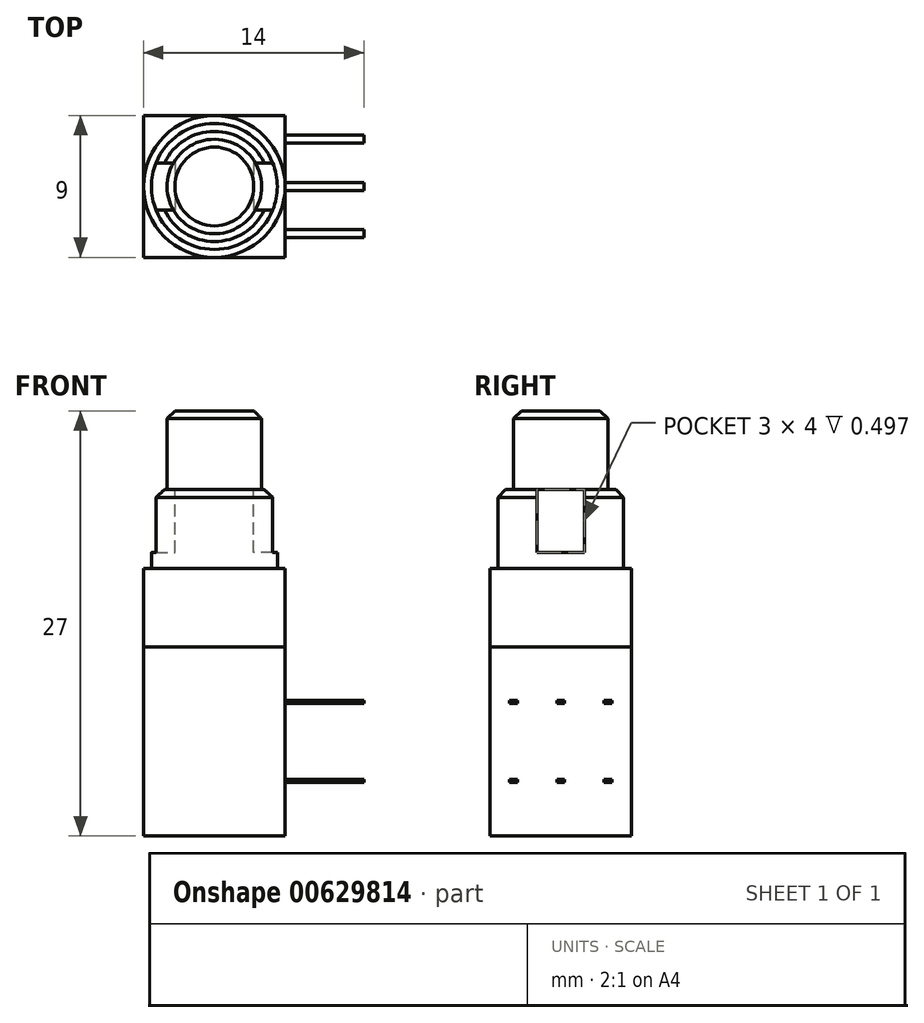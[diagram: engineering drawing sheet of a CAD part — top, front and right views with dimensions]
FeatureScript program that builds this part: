
annotation { "Feature Type Name" : "Feature", "Feature Type Description" : "" }
export const myFeature = defineFeature(function(context is Context, id is Id, definition is map)
    precondition{}
    {
        {
            var Q0;
            Q0=qCreatedBy(makeId("Top.planeOp"),FACE);
            var sketch = newSketch(context, id + "F0", { "sketchPlane" : qUnion([Q0])});
            skLineSegment(sketch, "E0.bottom", {"start": v(4.5, 4.5) * mm, "end": v(-4.5, 4.5) * mm});
            skLineSegment(sketch, "E0.top", {"start": v(4.5, -4.5) * mm, "end": v(-4.5, -4.5) * mm});
            skLineSegment(sketch, "E0.left", {"start": v(4.5, 4.5) * mm, "end": v(4.5, -4.5) * mm});
            skLineSegment(sketch, "E0.right", {"start": v(-4.5, 4.5) * mm, "end": v(-4.5, -4.5) * mm});
            skPoint(sketch, "E0.middle", {"position": v(0, 0) * mm});
            skSolve(sketch);
        }
        {
            var Q0;
            Q0=makeQuery(id+"F0.imprint","IMPRINT",FACE,{"disambiguationData":[TD([[makeQuery(id+"F0.imprint","IMPRINT",EDGE,{"derivedFrom":sQuery(id+"F0.wireOp",EDGE,"E0.bottom")}),1.0]])]});
            extrude(context, id + "F1", {"entities" : qUnion([Q0]), "depth" : 12 * mm, "offsetDistance" : 25 * mm});
        }
        {
            var Q0;
            Q0=makeQuery(id+"F1.opExtrude","CAP_FACE",FACE,{"disambiguationData":[OSD([sQuery(id+"F0.wireOp",EDGE,"E0.bottom"),sQuery(id+"F0.wireOp",EDGE,"E0.top"),sQuery(id+"F0.wireOp",EDGE,"E0.left"),sQuery(id+"F0.wireOp",EDGE,"E0.right")])],"isStart":false});
            var sketch = newSketch(context, id + "F2", { "sketchPlane" : qUnion([Q0])});
            skCircle(sketch, "E1", {"center": v(0, 0) * mm, "radius": 4.5 * mm});
            skSolve(sketch);
        }
        {
            var Q0;
            {var subQ0=sQuery(id+"F2.wireOp",EDGE,"E1");var subQ1=makeQuery(id+"F2.imprint","INTERSECT",VERTEX,{"derivedFrom":[makeQuery(id+"F1.opExtrude","CAP_EDGE",EDGE,{"disambiguationData":[OSD([sQuery(id+"F0.wireOp",EDGE,"E0.bottom")])],"isStart":false}),subQ0]});Q0=makeQuery(id+"F2.imprint","IMPRINT",FACE,{"disambiguationData":[TD([[makeQuery(id+"F2.imprint","IMPRINT",EDGE,{"disambiguationData":[TD([[subQ1,1.0]])],"derivedFrom":subQ0}),1.0]])]});}
            extrude(context, id + "F3", {"entities" : qUnion([Q0]), "operationType" : NewBodyOperationType.ADD, "depth" : 5 * mm, "offsetDistance" : 25 * mm});
        }
        {
            var Q0;
            Q0=makeQuery(id+"F3.opExtrude","CAP_FACE",FACE,{"disambiguationData":[OSD([sQuery(id+"F2.wireOp",EDGE,"E1")])],"isStart":false});
            var sketch = newSketch(context, id + "F4", { "sketchPlane" : qUnion([Q0])});
            skCircle(sketch, "E2", {"center": v(0, 0) * mm, "radius": 4 * mm});
            skSolve(sketch);
        }
        {
            var Q0;
            Q0=makeQuery(id+"F4.imprint","IMPRINT",FACE,{"disambiguationData":[TD([[makeQuery(id+"F4.imprint","IMPRINT",EDGE,{"derivedFrom":sQuery(id+"F4.wireOp",EDGE,"E2")}),1.0]])]});
            extrude(context, id + "F5", {"entities" : qUnion([Q0]), "operationType" : NewBodyOperationType.ADD, "depth" : 5 * mm, "offsetDistance" : 25 * mm});
        }
        {
            var Q0;
            Q0=makeQuery(id+"F5.opExtrude","CAP_FACE",FACE,{"disambiguationData":[OSD([sQuery(id+"F4.wireOp",EDGE,"E2")])],"isStart":false});
            var sketch = newSketch(context, id + "F6", { "sketchPlane" : qUnion([Q0])});
            skCircle(sketch, "E3.0", {"center": v(0, 0) * mm, "radius": 4 * mm});
            skLineSegment(sketch, "E4", {"start": v(-3.7, 1.5) * mm, "end": v(-2.5, 1.5) * mm});
            skLineSegment(sketch, "E5", {"start": v(-2.5, 1.5) * mm, "end": v(-2.5, -1.5) * mm});
            skLineSegment(sketch, "E6", {"start": v(-2.5, -1.5) * mm, "end": v(-3.7, -1.5) * mm});
            skLineSegment(sketch, "E7", {"start": v(3.7, 1.5) * mm, "end": v(2.5, 1.5) * mm});
            skLineSegment(sketch, "E8", {"start": v(2.5, 1.5) * mm, "end": v(2.5, -1.5) * mm});
            skLineSegment(sketch, "E9", {"start": v(2.5, -1.5) * mm, "end": v(3.7, -1.5) * mm});
            skSolve(sketch);
        }
        {
            var Q0;
            {var subQ0=sQuery(id+"F6.wireOp",EDGE,"E4");Q0=makeQuery(id+"F6.imprint","IMPRINT",FACE,{"disambiguationData":[TD([[makeQuery(id+"F6.imprint","IMPRINT",EDGE,{"derivedFrom":subQ0}),-1.0]])]});}
            var Q1;
            {var subQ0=sQuery(id+"F6.wireOp",EDGE,"E7");Q1=makeQuery(id+"F6.imprint","IMPRINT",FACE,{"disambiguationData":[TD([[makeQuery(id+"F6.imprint","IMPRINT",EDGE,{"derivedFrom":subQ0}),1.0]])]});}
            extrude(context, id + "F7", {"entities" : qUnion([Q0, Q1]), "operationType" : NewBodyOperationType.REMOVE, "oppositeDirection" : true, "depth" : 4 * mm, "offsetDistance" : 25 * mm});
        }
        {
            var Q0;
            Q0=makeQuery(id+"F5.opExtrude","CAP_FACE",FACE,{"disambiguationData":[OSD([sQuery(id+"F4.wireOp",EDGE,"E2")])],"isStart":false});
            var sketch = newSketch(context, id + "F8", { "sketchPlane" : qUnion([Q0])});
            skCircle(sketch, "E10", {"center": v(0, 0) * mm, "radius": 3 * mm});
            skSolve(sketch);
        }
        {
            var Q0;
            Q0 = qSketchRegion(id + "F8", true);
            extrude(context, id + "F9", {"entities" : qUnion([Q0]), "operationType" : NewBodyOperationType.ADD, "depth" : 5 * mm, "offsetDistance" : 25 * mm});
        }
        {
            var Q0;
            Q0=makeQuery(id+"F1.opExtrude","SWEPT_FACE",FACE,{"disambiguationData":[OSD([sQuery(id+"F0.wireOp",EDGE,"E0.left")])]});
            var sketch = newSketch(context, id + "F10", { "sketchPlane" : qUnion([Q0])});
            skLineSegment(sketch, "E11.bottom", {"start": v(-3, 8.5) * mm, "end": v(3, 8.5) * mm, "construction": true});
            skLineSegment(sketch, "E11.top", {"start": v(-3, 3.5) * mm, "end": v(3, 3.5) * mm, "construction": true});
            skLineSegment(sketch, "E11.left", {"start": v(-3, 8.5) * mm, "end": v(-3, 3.5) * mm, "construction": true});
            skLineSegment(sketch, "E11.right", {"start": v(3, 8.5) * mm, "end": v(3, 3.5) * mm, "construction": true});
            skLineSegment(sketch, "E12", {"start": v(0, 8.5) * mm, "end": v(0, 3.5) * mm, "construction": true});
            skLineSegment(sketch, "E13", {"start": v(0, 3.5) * mm, "end": v(0, 0) * mm, "construction": true});
            skLineSegment(sketch, "E14", {"start": v(3, 6) * mm, "end": v(4.5, 6) * mm, "construction": true});
            skLineSegment(sketch, "E15.bottom", {"start": v(-2.75, 8.4) * mm, "end": v(-3.25, 8.4) * mm});
            skLineSegment(sketch, "E15.top", {"start": v(-2.75, 8.6) * mm, "end": v(-3.25, 8.6) * mm});
            skLineSegment(sketch, "E15.left", {"start": v(-2.75, 8.4) * mm, "end": v(-2.75, 8.6) * mm});
            skLineSegment(sketch, "E15.right", {"start": v(-3.25, 8.4) * mm, "end": v(-3.25, 8.6) * mm});
            skPoint(sketch, "E15.middle", {"position": v(-3, 8.5) * mm});
            skLineSegment(sketch, "E16.bottom", {"start": v(0.25, 8.4) * mm, "end": v(-0.25, 8.4) * mm});
            skLineSegment(sketch, "E16.top", {"start": v(0.25, 8.6) * mm, "end": v(-0.25, 8.6) * mm});
            skLineSegment(sketch, "E16.left", {"start": v(0.25, 8.4) * mm, "end": v(0.25, 8.6) * mm});
            skLineSegment(sketch, "E16.right", {"start": v(-0.25, 8.4) * mm, "end": v(-0.25, 8.6) * mm});
            skPoint(sketch, "E16.middle", {"position": v(0, 8.5) * mm});
            skLineSegment(sketch, "E17.bottom", {"start": v(2.75, 8.4) * mm, "end": v(3.25, 8.4) * mm});
            skLineSegment(sketch, "E17.top", {"start": v(2.75, 8.6) * mm, "end": v(3.25, 8.6) * mm});
            skLineSegment(sketch, "E17.left", {"start": v(2.75, 8.4) * mm, "end": v(2.75, 8.6) * mm});
            skLineSegment(sketch, "E17.right", {"start": v(3.25, 8.4) * mm, "end": v(3.25, 8.6) * mm});
            skPoint(sketch, "E17.middle", {"position": v(3, 8.5) * mm});
            skLineSegment(sketch, "E18.bottom", {"start": v(-3.25, 3.4) * mm, "end": v(-2.75, 3.4) * mm});
            skLineSegment(sketch, "E18.top", {"start": v(-3.25, 3.6) * mm, "end": v(-2.75, 3.6) * mm});
            skLineSegment(sketch, "E18.left", {"start": v(-3.25, 3.4) * mm, "end": v(-3.25, 3.6) * mm});
            skLineSegment(sketch, "E18.right", {"start": v(-2.75, 3.4) * mm, "end": v(-2.75, 3.6) * mm});
            skPoint(sketch, "E18.middle", {"position": v(-3, 3.5) * mm});
            skLineSegment(sketch, "E19.bottom", {"start": v(-0.25, 3.4) * mm, "end": v(0.25, 3.4) * mm});
            skLineSegment(sketch, "E19.top", {"start": v(-0.25, 3.6) * mm, "end": v(0.25, 3.6) * mm});
            skLineSegment(sketch, "E19.left", {"start": v(-0.25, 3.4) * mm, "end": v(-0.25, 3.6) * mm});
            skLineSegment(sketch, "E19.right", {"start": v(0.25, 3.4) * mm, "end": v(0.25, 3.6) * mm});
            skPoint(sketch, "E19.middle", {"position": v(0, 3.5) * mm});
            skLineSegment(sketch, "E20.bottom", {"start": v(3.25, 3.4) * mm, "end": v(2.75, 3.4) * mm});
            skLineSegment(sketch, "E20.top", {"start": v(3.25, 3.6) * mm, "end": v(2.75, 3.6) * mm});
            skLineSegment(sketch, "E20.left", {"start": v(3.25, 3.4) * mm, "end": v(3.25, 3.6) * mm});
            skLineSegment(sketch, "E20.right", {"start": v(2.75, 3.4) * mm, "end": v(2.75, 3.6) * mm});
            skPoint(sketch, "E20.middle", {"position": v(3, 3.5) * mm});
            skSolve(sketch);
        }
        {
            var Q0;
            Q0 = qSketchRegion(id + "F10", true);
            extrude(context, id + "F11", {"entities" : qUnion([Q0]), "operationType" : NewBodyOperationType.ADD, "depth" : 5 * mm, "offsetDistance" : 25 * mm});
        }
        {
            var Q0;
            Q0=makeQuery(id+"F9.opExtrude","CAP_EDGE",EDGE,{"disambiguationData":[OSD([sQuery(id+"F8.wireOp",EDGE,"E10")])],"isStart":false});
            var Q1;
            {var subQ0=sQuery(id+"F4.wireOp",EDGE,"E2");Q1=makeQuery(id+"F7.boolean.opBoolean","SPLIT",EDGE,{"disambiguationData":[TD([makeQuery(id+"F7.opExtrude","SWEPT_FACE",FACE,{"disambiguationData":[OSD([sQuery(id+"F6.wireOp",EDGE,"E4")])]})])],"derivedFrom":makeQuery(id+"F5.opExtrude","CAP_EDGE",EDGE,{"disambiguationData":[OSD([subQ0])],"isStart":false})});}
            var Q2;
            {var subQ0=sQuery(id+"F4.wireOp",EDGE,"E2");Q2=makeQuery(id+"F7.boolean.opBoolean","SPLIT",EDGE,{"disambiguationData":[TD([makeQuery(id+"F7.opExtrude","SWEPT_FACE",FACE,{"disambiguationData":[OSD([sQuery(id+"F6.wireOp",EDGE,"E6")])]})])],"derivedFrom":makeQuery(id+"F5.opExtrude","CAP_EDGE",EDGE,{"disambiguationData":[OSD([subQ0])],"isStart":false})});}
            chamfer(context, id + "F12", {"entities" : qUnion([Q0, Q1, Q2]), "width" : 0.5 * mm, "tangentPropagation" : true});
        }
    });
